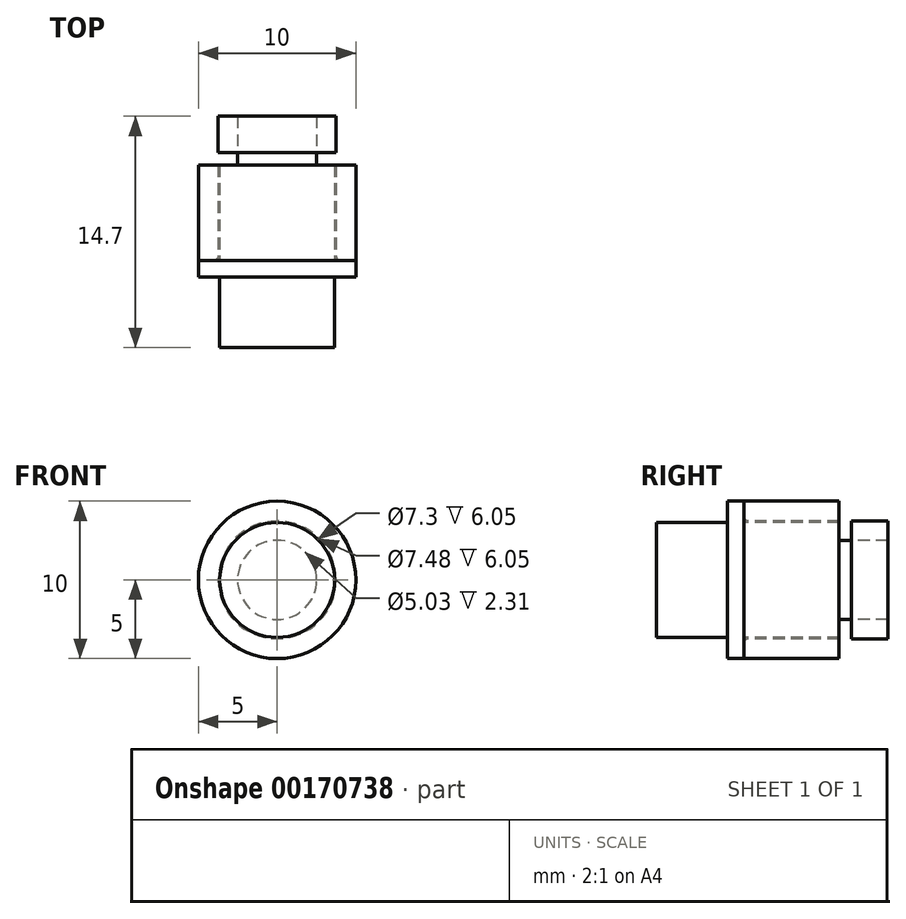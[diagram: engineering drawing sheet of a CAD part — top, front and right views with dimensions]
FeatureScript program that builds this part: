
annotation { "Feature Type Name" : "Feature", "Feature Type Description" : "" }
export const myFeature = defineFeature(function(context is Context, id is Id, definition is map)
    precondition{}
    {
        {
            var Q0;
            Q0=qCreatedBy(makeId("Front.planeOp"),FACE);
            var sketch = newSketch(context, id + "F0", { "sketchPlane" : qUnion([Q0])});
            skCircle(sketch, "E0", {"center": v(0, 0) * mm, "radius": 3.65 * mm});
            skSolve(sketch);
        }
        {
            var Q0;
            Q0=makeQuery(id+"F0.imprint","IMPRINT",FACE,{"disambiguationData":[TD([[makeQuery(id+"F0.imprint","IMPRINT",EDGE,{"derivedFrom":sQuery(id+"F0.wireOp",EDGE,"E0")}),1.0]])]});
            extrude(context, id + "F1", {"entities" : qUnion([Q0]), "oppositeDirection" : true, "depth" : 4.5 * mm});
        }
        {
            var Q0;
            Q0=makeQuery(id+"F1.opExtrude","CAP_FACE",FACE,{"disambiguationData":[OSD([sQuery(id+"F0.wireOp",EDGE,"E0")])],"isStart":false});
            var sketch = newSketch(context, id + "F2", { "sketchPlane" : qUnion([Q0])});
            skCircle(sketch, "E1", {"center": v(0, 0) * mm, "radius": 5 * mm});
            skSolve(sketch);
        }
        {
            var Q0;
            Q0=makeQuery(id+"F2.imprint","IMPRINT",FACE,{"disambiguationData":[TD([[makeQuery(id+"F2.imprint","IMPRINT",EDGE,{"derivedFrom":sQuery(id+"F2.wireOp",EDGE,"E1")}),1.0]])]});
            extrude(context, id + "F3", {"entities" : qUnion([Q0]), "depth" : 1.05 * mm});
        }
        {
            var Q0;
            Q0=makeQuery(id+"F1.opExtrude","CAP_FACE",FACE,{"disambiguationData":[OSD([sQuery(id+"F0.wireOp",EDGE,"E0")])],"isStart":false});
            var sketch = newSketch(context, id + "F4", { "sketchPlane" : qUnion([Q0])});
            skSolve(sketch);
        }
        {
            var Q0;
            Q0 = qSketchRegion(id + "F4", true);
            var Q1;
            Q1=makeQuery(id+"F4.imprint","IMPRINT",FACE,{"disambiguationData":[TD([[makeQuery(id+"F4.imprint","IMPRINT",EDGE,{"derivedFrom":makeQuery(id+"F1.opExtrude","CAP_EDGE",EDGE,{"disambiguationData":[OSD([sQuery(id+"F0.wireOp",EDGE,"E0")])],"isStart":false})}),-1.0]])]});
            extrude(context, id + "F5", {"entities" : qUnion([Q0, Q1]), "depth" : 1.05 * mm});
        }
        {
            var Q0;
            Q0=makeQuery(id+"F5.opExtrude","CAP_FACE",FACE,{"disambiguationData":[OSD([sQuery(id+"F0.wireOp",EDGE,"E0")])],"isStart":false});
            var sketch = newSketch(context, id + "F6", { "sketchPlane" : qUnion([Q0])});
            skCircle(sketch, "E2", {"center": v(0, 0) * mm, "radius": 3.74 * mm});
            skSolve(sketch);
        }
        {
            var Q0;
            Q0=makeQuery(id+"F6.imprint","IMPRINT",FACE,{"disambiguationData":[TD([[makeQuery(id+"F6.imprint","IMPRINT",EDGE,{"derivedFrom":sQuery(id+"F6.wireOp",EDGE,"E2")}),1.0]])]});
            extrude(context, id + "F7", {"entities" : qUnion([Q0]), "operationType" : NewBodyOperationType.ADD, "depth" : 6.05 * mm});
        }
        {
            var Q0;
            Q0=makeQuery(id+"F5.opExtrude","CAP_FACE",FACE,{"disambiguationData":[OSD([sQuery(id+"F0.wireOp",EDGE,"E0")])],"isStart":false});
            extrude(context, id + "F8", {"entities" : qUnion([Q0]), "depth" : 6.05 * mm});
        }
        {
            var Q0;
            Q0=makeQuery(id+"F8.opExtrude","CAP_FACE",FACE,{"disambiguationData":[OSD([sQuery(id+"F0.wireOp",EDGE,"E0")])],"isStart":false});
            var sketch = newSketch(context, id + "F9", { "sketchPlane" : qUnion([Q0])});
            skCircle(sketch, "E3", {"center": v(0, 0) * mm, "radius": 2.51 * mm});
            skSolve(sketch);
        }
        {
            var Q0;
            Q0=makeQuery(id+"F9.imprint","IMPRINT",FACE,{"disambiguationData":[TD([[makeQuery(id+"F9.imprint","IMPRINT",EDGE,{"derivedFrom":sQuery(id+"F9.wireOp",EDGE,"E3")}),1.0]])]});
            extrude(context, id + "F10", {"entities" : qUnion([Q0]), "operationType" : NewBodyOperationType.ADD, "depth" : 0.79 * mm});
        }
        {
            var Q0;
            Q0=makeQuery(id+"F10.opExtrude","CAP_FACE",FACE,{"disambiguationData":[OSD([sQuery(id+"F9.wireOp",EDGE,"E3")])],"isStart":false});
            var sketch = newSketch(context, id + "F11", { "sketchPlane" : qUnion([Q0])});
            skCircle(sketch, "E4", {"center": v(0, 0) * mm, "radius": 3.74 * mm});
            skSolve(sketch);
        }
        {
            var Q0;
            Q0=makeQuery(id+"F11.imprint","IMPRINT",FACE,{"disambiguationData":[TD([[makeQuery(id+"F11.imprint","IMPRINT",EDGE,{"derivedFrom":sQuery(id+"F11.wireOp",EDGE,"E4")}),1.0]])]});
            extrude(context, id + "F12", {"entities" : qUnion([Q0]), "depth" : 2.31 * mm});
        }
        {
            var Q0;
            Q0=makeQuery(id+"F10.opExtrude","CAP_FACE",FACE,{"disambiguationData":[OSD([sQuery(id+"F9.wireOp",EDGE,"E3")])],"isStart":false});
            var sketch = newSketch(context, id + "F13", { "sketchPlane" : qUnion([Q0])});
            skSolve(sketch);
        }
        {
            var Q0;
            Q0=makeQuery(id+"F13.imprint","IMPRINT",FACE,{"disambiguationData":[TD([[makeQuery(id+"F13.imprint","IMPRINT",EDGE,{"derivedFrom":makeQuery(id+"F10.opExtrude","CAP_EDGE",EDGE,{"disambiguationData":[OSD([sQuery(id+"F9.wireOp",EDGE,"E3")])],"isStart":false})}),1.0]])]});
            extrude(context, id + "F14", {"entities" : qUnion([Q0]), "depth" : 2.31 * mm});
        }
        {
            var Q0;
            Q0=makeQuery(id+"F7.opExtrude","CAP_EDGE",EDGE,{"disambiguationData":[OSD([sQuery(id+"F6.wireOp",EDGE,"E2")])],"isStart":true});
            fillet(context, id + "F15", {"entities" : qUnion([Q0]), "radius" : 0.3 * mm, "tangentPropagation" : true, "allowEdgeOverflow" : false});
        }
    });
